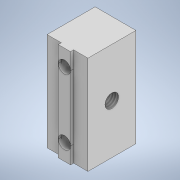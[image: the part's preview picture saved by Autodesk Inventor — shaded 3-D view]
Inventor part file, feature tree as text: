
AUTODESK INVENTOR PART (.ipt)
format: ipt  version: 2021 (Build 250183000, 183)  size: 140,800 bytes
history: native  units: mm
features: sketch x5, projected_geometry x4, extrude x3, hole x1
ambient origin geometry x8: Origin, YZ Plane, XZ Plane, XY Plane, X Axis, Y Axis, Z Axis, Center Point
bodies: Solid1 (feature_tree)
feature tree (13):
  extrude  "Extrusion1"  Depth=48.0mm
  extrude  "Extrusion2"  Depth=3.0mm
  sketch  "Sketch3"  dims[d5=3.0mm d6=1.5mm d7=0.0mm]
  hole  "Hole1"  [1 undecoded]
  extrude  "Extrusion3"  Depth=6.0mm
  sketch  "Sketch1"  dims[d0=20.0mm d1=48.0mm]
  sketch  "Sketch2"  dims[d2=25.0mm d3=0.0mm d4=3.0mm]
  projected_geometry  "Projected Loop1"
  projected_geometry  "Projected Loop2"
  projected_geometry  "Projected Loop3"
  sketch  "Sketch4"  dims[d8=6.647mm d9=16.0mm d10=4.0mm d11=2.0mm d12=90.0deg d13=8.0mm d14=20.594885mm d15=6.0mm]
  sketch  "Sketch5"  dims[d16=6.0mm d17=8.0mm d18=8.0mm d19=0.0mm d20=0.0mm]
  projected_geometry  "Projected Loop4"
note: 1 required parameter value undecoded (feature->parameter linkage not recoverable at this tier; creation-order binding heuristic only, values carry confidence <= 0.55)
